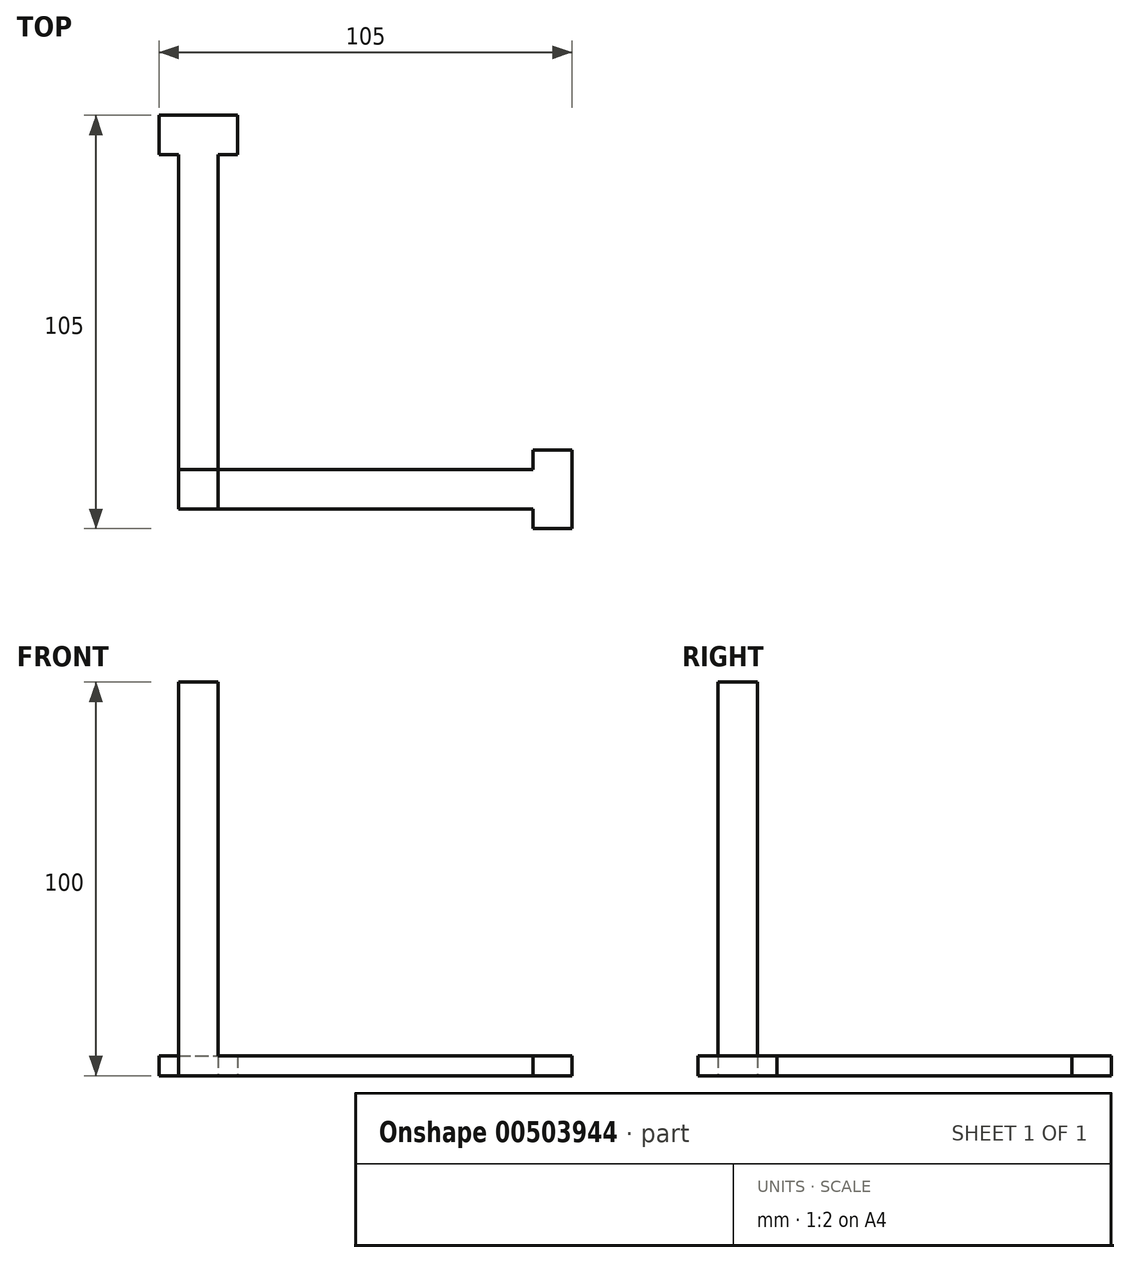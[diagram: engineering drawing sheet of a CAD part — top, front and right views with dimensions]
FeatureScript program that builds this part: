
annotation { "Feature Type Name" : "Feature", "Feature Type Description" : "" }
export const myFeature = defineFeature(function(context is Context, id is Id, definition is map)
    precondition{}
    {
        {
            var Q0;
            Q0=qCreatedBy(makeId("Top.planeOp"),FACE);
            var sketch = newSketch(context, id + "F0", { "sketchPlane" : qUnion([Q0])});
            skLineSegment(sketch, "E0", {"start": v(-15, 90) * mm, "end": v(5, 90) * mm});
            skLineSegment(sketch, "E1", {"start": v(5, 90) * mm, "end": v(5, 80) * mm});
            skLineSegment(sketch, "E2", {"start": v(5, 80) * mm, "end": v(0, 80) * mm});
            skLineSegment(sketch, "E3", {"start": v(0, 80) * mm, "end": v(0, 0) * mm});
            skLineSegment(sketch, "E4", {"start": v(0, 0) * mm, "end": v(80, 0) * mm});
            skLineSegment(sketch, "E5", {"start": v(80, 0) * mm, "end": v(80, 5) * mm});
            skLineSegment(sketch, "E6", {"start": v(80, 5) * mm, "end": v(90, 5) * mm});
            skLineSegment(sketch, "E7", {"start": v(90, 5) * mm, "end": v(90, -15) * mm});
            skLineSegment(sketch, "E8", {"start": v(90, -15) * mm, "end": v(80, -15) * mm});
            skLineSegment(sketch, "E9", {"start": v(80, -15) * mm, "end": v(80, -10) * mm});
            skLineSegment(sketch, "E10", {"start": v(80, -10) * mm, "end": v(-10, -10) * mm});
            skLineSegment(sketch, "E11", {"start": v(-10, -10) * mm, "end": v(-10, 80) * mm});
            skLineSegment(sketch, "E12", {"start": v(-10, 80) * mm, "end": v(-15, 80) * mm});
            skLineSegment(sketch, "E13", {"start": v(-15, 80) * mm, "end": v(-15, 90) * mm});
            skSolve(sketch);
        }
        {
            var Q0;
            Q0=makeQuery(id+"F0.imprint","IMPRINT",FACE,{"disambiguationData":[TD([[makeQuery(id+"F0.imprint","IMPRINT",EDGE,{"derivedFrom":sQuery(id+"F0.wireOp",EDGE,"E0")}),-1.0]])]});
            extrude(context, id + "F1", {"entities" : qUnion([Q0]), "depth" : 5 * mm, "offsetDistance" : 25 * mm});
        }
        {
            var Q0;
            Q0=makeQuery(id+"F1.opExtrude","CAP_FACE",FACE,{"disambiguationData":[OSD([sQuery(id+"F0.wireOp",EDGE,"E0"),sQuery(id+"F0.wireOp",EDGE,"E1"),sQuery(id+"F0.wireOp",EDGE,"E2"),sQuery(id+"F0.wireOp",EDGE,"E3"),sQuery(id+"F0.wireOp",EDGE,"E4"),sQuery(id+"F0.wireOp",EDGE,"E5"),sQuery(id+"F0.wireOp",EDGE,"E6"),sQuery(id+"F0.wireOp",EDGE,"E7"),sQuery(id+"F0.wireOp",EDGE,"E8"),sQuery(id+"F0.wireOp",EDGE,"E9"),sQuery(id+"F0.wireOp",EDGE,"E10"),sQuery(id+"F0.wireOp",EDGE,"E11"),sQuery(id+"F0.wireOp",EDGE,"E12"),sQuery(id+"F0.wireOp",EDGE,"E13")])],"isStart":false});
            var sketch = newSketch(context, id + "F2", { "sketchPlane" : qUnion([Q0])});
            skLineSegment(sketch, "E14.bottom", {"start": v(-10, -10) * mm, "end": v(0, -10) * mm});
            skLineSegment(sketch, "E14.top", {"start": v(-10, 0) * mm, "end": v(0, 0) * mm});
            skLineSegment(sketch, "E14.left", {"start": v(-10, -10) * mm, "end": v(-10, 0) * mm});
            skLineSegment(sketch, "E14.right", {"start": v(0, -10) * mm, "end": v(0, 0) * mm});
            skSolve(sketch);
        }
        {
            var Q0;
            Q0=makeQuery(id+"F2.imprint","IMPRINT",FACE,{"disambiguationData":[TD([[makeQuery(id+"F2.imprint","IMPRINT",EDGE,{"derivedFrom":sQuery(id+"F2.wireOp",EDGE,"E14.bottom")}),-1.0]])]});
            extrude(context, id + "F3", {"entities" : qUnion([Q0]), "operationType" : NewBodyOperationType.ADD, "depth" : 95 * mm, "offsetDistance" : 25 * mm});
        }
    });
